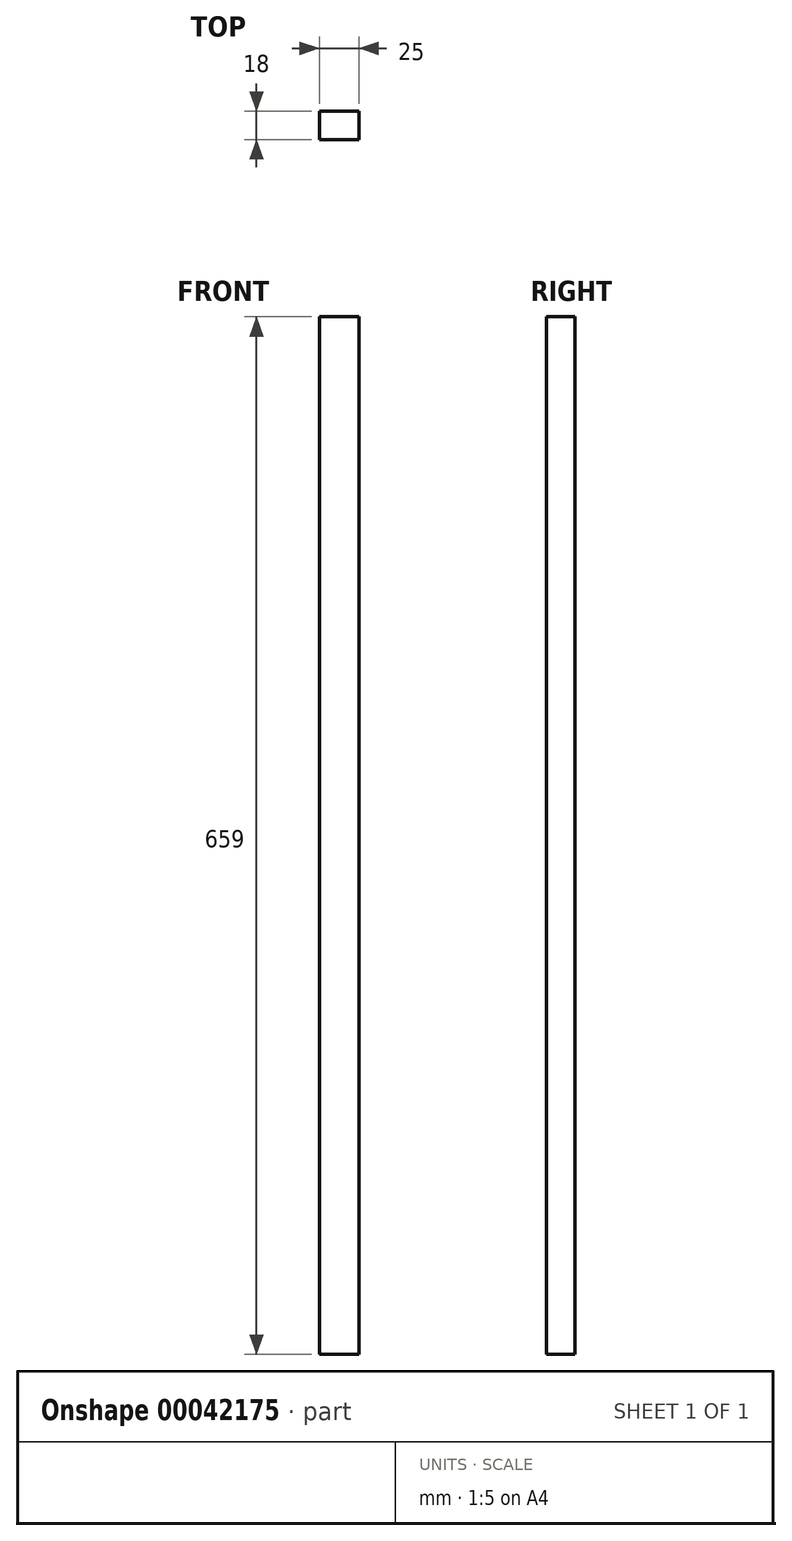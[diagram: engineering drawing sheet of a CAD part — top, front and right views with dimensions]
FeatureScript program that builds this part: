
annotation { "Feature Type Name" : "Feature", "Feature Type Description" : "" }
export const myFeature = defineFeature(function(context is Context, id is Id, definition is map)
    precondition{}
    {
        {
            var Q0;
            Q0=qCreatedBy(makeId("Top.planeOp"),FACE);
            var sketch = newSketch(context, id + "F0", { "sketchPlane" : qUnion([Q0])});
            skLineSegment(sketch, "E0.bottom", {"start": v(0, 0) * mm, "end": v(25, 0) * mm});
            skLineSegment(sketch, "E0.top", {"start": v(0, 18) * mm, "end": v(25, 18) * mm});
            skLineSegment(sketch, "E0.left", {"start": v(0, 0) * mm, "end": v(0, 18) * mm});
            skLineSegment(sketch, "E0.right", {"start": v(25, 0) * mm, "end": v(25, 18) * mm});
            skSolve(sketch);
        }
        {
            var Q0;
            Q0=makeQuery(id+"F0.imprint","IMPRINT",FACE,{"disambiguationData":[TD([[makeQuery(id+"F0.imprint","IMPRINT",EDGE,{"derivedFrom":sQuery(id+"F0.wireOp",EDGE,"E0.bottom")}),1.0]])]});
            extrude(context, id + "F1", {"entities" : qUnion([Q0]), "depth" : 659 * mm});
        }
    });
